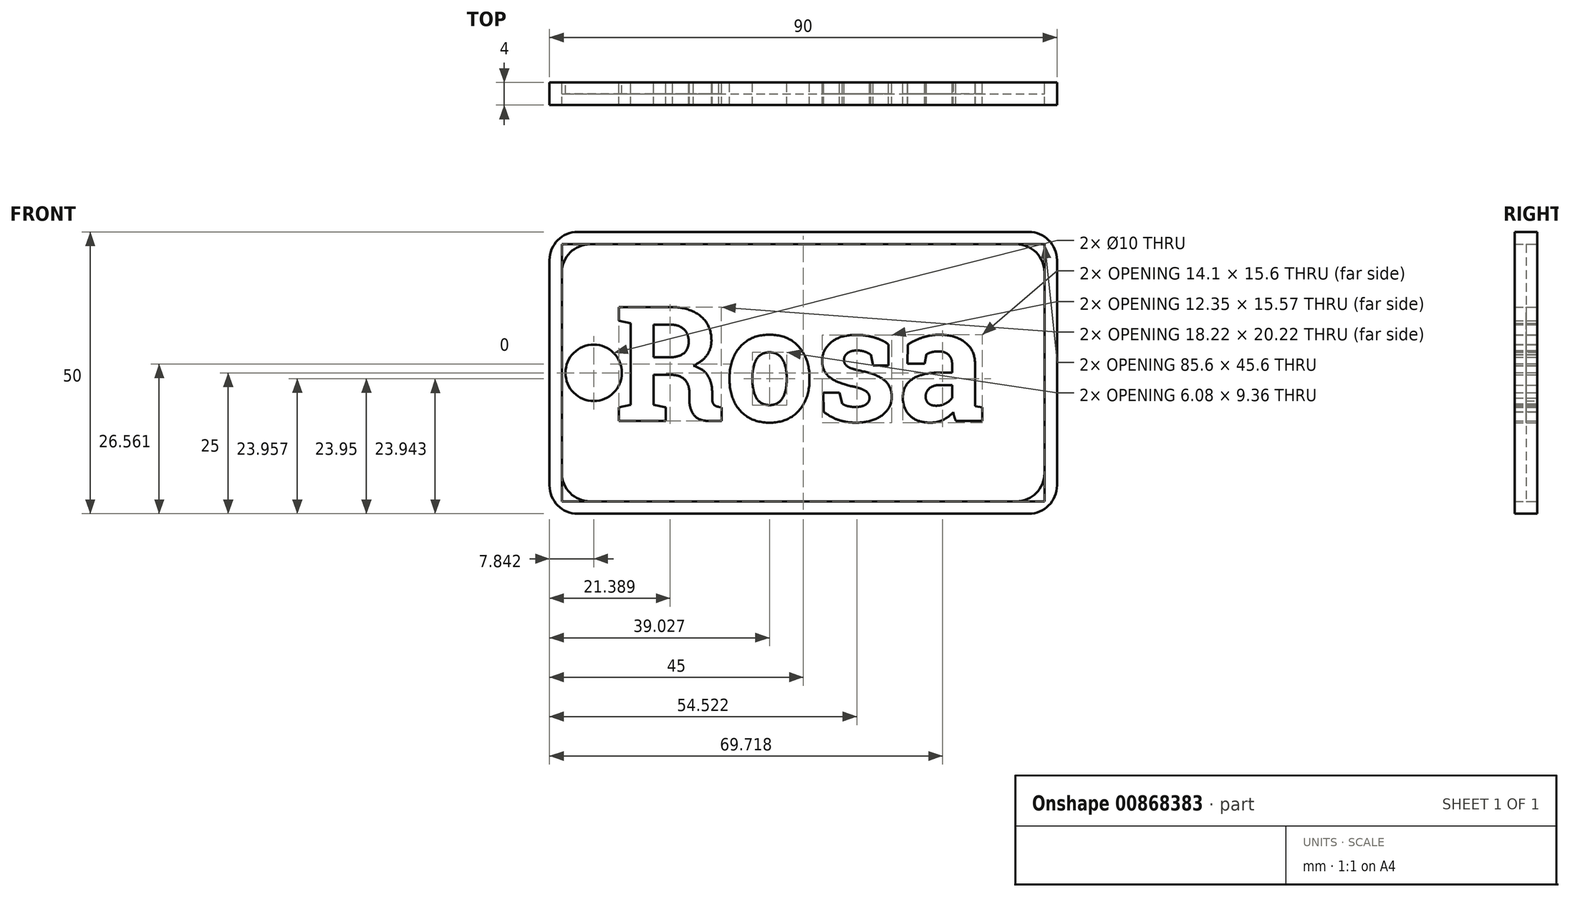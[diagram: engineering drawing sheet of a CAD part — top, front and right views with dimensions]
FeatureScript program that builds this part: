
annotation { "Feature Type Name" : "Feature", "Feature Type Description" : "" }
export const myFeature = defineFeature(function(context is Context, id is Id, definition is map)
    precondition{}
    {
        {
            var Q0;
            Q0=qCreatedBy(makeId("Front.planeOp"),FACE);
            var sketch = newSketch(context, id + "F0", { "sketchPlane" : qUnion([Q0])});
            skLineSegment(sketch, "E0.bottom", {"start": v(-45, 25) * mm, "end": v(45, 25) * mm});
            skLineSegment(sketch, "E0.top", {"start": v(-45, -25) * mm, "end": v(45, -25) * mm});
            skLineSegment(sketch, "E0.left", {"start": v(-45, 25) * mm, "end": v(-45, -25) * mm});
            skLineSegment(sketch, "E0.right", {"start": v(45, 25) * mm, "end": v(45, -25) * mm});
            skLineSegment(sketch, "E1.0", {"start": v(-42.8, 22.8) * mm, "end": v(42.8, 22.8) * mm});
            skLineSegment(sketch, "E1.1", {"start": v(-42.8, 22.8) * mm, "end": v(-42.8, -22.8) * mm});
            skLineSegment(sketch, "E1.2", {"start": v(-42.8, -22.8) * mm, "end": v(42.8, -22.8) * mm});
            skLineSegment(sketch, "E1.3", {"start": v(42.8, 22.8) * mm, "end": v(42.8, -22.8) * mm});
            skText(sketch, "E2", { "text": "Rosa", "fontName": "RobotoSlab-Bold.ttf"});
            skCircle(sketch, "E3", {"center": v(-37.16, 0) * mm, "radius": 5 * mm});
            const initialGuessF0  = {"E2": [-0.0335, -0.00855, 1, 0, 0.02048]};
            skSetInitialGuess(sketch, initialGuessF0);
            skSolve(sketch);
        }
        {
            var Q0;
            Q0=makeQuery(id+"F0.imprint","IMPRINT",FACE,{"disambiguationData":[TD([[makeQuery(id+"F0.imprint","IMPRINT",EDGE,{"derivedFrom":sQuery(id+"F0.wireOp",EDGE,"E2.sketch_text.stroke-244")}),1.0]])]});
            var Q1;
            Q1=makeQuery(id+"F0.imprint","IMPRINT",FACE,{"disambiguationData":[TD([[makeQuery(id+"F0.imprint","IMPRINT",EDGE,{"derivedFrom":sQuery(id+"F0.wireOp",EDGE,"E2.sketch_text.stroke-218")}),1.0]])]});
            var Q2;
            Q2=makeQuery(id+"F0.imprint","IMPRINT",FACE,{"disambiguationData":[TD([[makeQuery(id+"F0.imprint","IMPRINT",EDGE,{"derivedFrom":sQuery(id+"F0.wireOp",EDGE,"E1.0")}),-1.0]])]});
            var Q3;
            Q3=makeQuery(id+"F0.imprint","IMPRINT",FACE,{"disambiguationData":[TD([[makeQuery(id+"F0.imprint","IMPRINT",EDGE,{"derivedFrom":sQuery(id+"F0.wireOp",EDGE,"E2.sketch_text.stroke-36")}),-1.0]])]});
            var Q4;
            Q4=makeQuery(id+"F0.imprint","IMPRINT",FACE,{"disambiguationData":[TD([[makeQuery(id+"F0.imprint","IMPRINT",EDGE,{"derivedFrom":sQuery(id+"F0.wireOp",EDGE,"E2.sketch_text.stroke-46")}),1.0]])]});
            var Q5;
            Q5=makeQuery(id+"F0.imprint","IMPRINT",FACE,{"disambiguationData":[TD([[makeQuery(id+"F0.imprint","IMPRINT",EDGE,{"derivedFrom":sQuery(id+"F0.wireOp",EDGE,"E2.sketch_text.stroke-29")}),1.0]])]});
            var Q6;
            Q6=makeQuery(id+"F0.imprint","IMPRINT",FACE,{"disambiguationData":[TD([[makeQuery(id+"F0.imprint","IMPRINT",EDGE,{"derivedFrom":sQuery(id+"F0.wireOp",EDGE,"E2.sketch_text.stroke-113")}),1.0]])]});
            extrude(context, id + "F1", {"entities" : qUnion([Q0, Q1, Q2, Q3, Q4, Q5, Q6]), "depth" : 2 * mm, "offsetDistance" : 25 * mm});
        }
        {
            var Q0;
            Q0=makeQuery(id+"F0.imprint","IMPRINT",FACE,{"disambiguationData":[TD([[makeQuery(id+"F0.imprint","IMPRINT",EDGE,{"derivedFrom":sQuery(id+"F0.wireOp",EDGE,"E2.sketch_text.stroke-0")}),-1.0]])]});
            var Q1;
            Q1=makeQuery(id+"F0.imprint","IMPRINT",FACE,{"disambiguationData":[TD([[makeQuery(id+"F0.imprint","IMPRINT",EDGE,{"derivedFrom":sQuery(id+"F0.wireOp",EDGE,"E2.sketch_text.stroke-20")}),-1.0]])]});
            var Q2;
            Q2=makeQuery(id+"F0.imprint","IMPRINT",FACE,{"disambiguationData":[TD([[makeQuery(id+"F0.imprint","IMPRINT",EDGE,{"derivedFrom":sQuery(id+"F0.wireOp",EDGE,"E2.sketch_text.stroke-63")}),-1.0]])]});
            var Q3;
            Q3=makeQuery(id+"F0.imprint","IMPRINT",FACE,{"disambiguationData":[TD([[makeQuery(id+"F0.imprint","IMPRINT",EDGE,{"derivedFrom":sQuery(id+"F0.wireOp",EDGE,"E2.sketch_text.stroke-98")}),-1.0]])]});
            var Q4;
            Q4=makeQuery(id+"F0.imprint","IMPRINT",FACE,{"disambiguationData":[TD([[makeQuery(id+"F0.imprint","IMPRINT",EDGE,{"derivedFrom":sQuery(id+"F0.wireOp",EDGE,"E2.sketch_text.stroke-117")}),-1.0]])]});
            var Q5;
            Q5=makeQuery(id+"F0.imprint","IMPRINT",FACE,{"disambiguationData":[TD([[makeQuery(id+"F0.imprint","IMPRINT",EDGE,{"derivedFrom":sQuery(id+"F0.wireOp",EDGE,"E2.sketch_text.stroke-127")}),-1.0]])]});
            var Q6;
            Q6=makeQuery(id+"F0.imprint","IMPRINT",FACE,{"disambiguationData":[TD([[makeQuery(id+"F0.imprint","IMPRINT",EDGE,{"derivedFrom":sQuery(id+"F0.wireOp",EDGE,"E2.sketch_text.stroke-131")}),-1.0]])]});
            var Q7;
            Q7=makeQuery(id+"F0.imprint","IMPRINT",FACE,{"disambiguationData":[TD([[makeQuery(id+"F0.imprint","IMPRINT",EDGE,{"derivedFrom":sQuery(id+"F0.wireOp",EDGE,"E2.sketch_text.stroke-141")}),-1.0]])]});
            var Q8;
            Q8=makeQuery(id+"F0.imprint","IMPRINT",FACE,{"disambiguationData":[TD([[makeQuery(id+"F0.imprint","IMPRINT",EDGE,{"derivedFrom":sQuery(id+"F0.wireOp",EDGE,"E2.sketch_text.stroke-151")}),-1.0]])]});
            var Q9;
            Q9=makeQuery(id+"F0.imprint","IMPRINT",FACE,{"disambiguationData":[TD([[makeQuery(id+"F0.imprint","IMPRINT",EDGE,{"derivedFrom":sQuery(id+"F0.wireOp",EDGE,"E2.sketch_text.stroke-254")}),-1.0]])]});
            var Q10;
            Q10=makeQuery(id+"F0.imprint","IMPRINT",FACE,{"disambiguationData":[TD([[makeQuery(id+"F0.imprint","IMPRINT",EDGE,{"derivedFrom":sQuery(id+"F0.wireOp",EDGE,"E2.sketch_text.stroke-225")}),-1.0]])]});
            var Q11;
            Q11=makeQuery(id+"F0.imprint","IMPRINT",FACE,{"disambiguationData":[TD([[makeQuery(id+"F0.imprint","IMPRINT",EDGE,{"derivedFrom":sQuery(id+"F0.wireOp",EDGE,"E2.sketch_text.stroke-201")}),-1.0]])]});
            var Q12;
            Q12=makeQuery(id+"F0.imprint","IMPRINT",FACE,{"disambiguationData":[TD([[makeQuery(id+"F0.imprint","IMPRINT",EDGE,{"derivedFrom":sQuery(id+"F0.wireOp",EDGE,"E2.sketch_text.stroke-171")}),-1.0]])]});
            var Q13;
            Q13=makeQuery(id+"F0.imprint","IMPRINT",FACE,{"disambiguationData":[TD([[makeQuery(id+"F0.imprint","IMPRINT",EDGE,{"derivedFrom":sQuery(id+"F0.wireOp",EDGE,"E0.bottom")}),-1.0]])]});
            var Q14;
            Q14=makeQuery(id+"F0.imprint","IMPRINT",FACE,{"disambiguationData":[TD([[makeQuery(id+"F0.imprint","IMPRINT",EDGE,{"derivedFrom":sQuery(id+"F0.wireOp",EDGE,"E2.sketch_text.stroke-36")}),-1.0]])]});
            extrude(context, id + "F2", {"entities" : qUnion([Q0, Q1, Q2, Q3, Q4, Q5, Q6, Q7, Q8, Q9, Q10, Q11, Q12, Q13, Q14]), "depth" : 4 * mm, "offsetDistance" : 25 * mm});
        }
        {
            var Q0;
            Q0=makeQuery(id+"F2.opExtrude","SWEPT_EDGE",EDGE,{"disambiguationData":[OSD([sQuery(id+"F0.wireOp",EDGE,"E0.top"),sQuery(id+"F0.wireOp",EDGE,"E0.left")])]});
            var Q1;
            Q1=makeQuery(id+"F2.opExtrude","SWEPT_EDGE",EDGE,{"disambiguationData":[OSD([sQuery(id+"F0.wireOp",EDGE,"E0.bottom"),sQuery(id+"F0.wireOp",EDGE,"E0.left")])]});
            var Q2;
            Q2=makeQuery(id+"F2.opExtrude","SWEPT_EDGE",EDGE,{"disambiguationData":[OSD([sQuery(id+"F0.wireOp",EDGE,"E1.1"),sQuery(id+"F0.wireOp",EDGE,"E1.2")])]});
            var Q3;
            Q3=makeQuery(id+"F2.opExtrude","SWEPT_EDGE",EDGE,{"disambiguationData":[OSD([sQuery(id+"F0.wireOp",EDGE,"E1.0"),sQuery(id+"F0.wireOp",EDGE,"E1.1")])]});
            var Q4;
            Q4=makeQuery(id+"F2.opExtrude","SWEPT_EDGE",EDGE,{"disambiguationData":[OSD([sQuery(id+"F0.wireOp",EDGE,"E1.0"),sQuery(id+"F0.wireOp",EDGE,"E1.3")])]});
            var Q5;
            Q5=makeQuery(id+"F2.opExtrude","SWEPT_EDGE",EDGE,{"disambiguationData":[OSD([sQuery(id+"F0.wireOp",EDGE,"E1.2"),sQuery(id+"F0.wireOp",EDGE,"E1.3")])]});
            var Q6;
            Q6=makeQuery(id+"F2.opExtrude","SWEPT_EDGE",EDGE,{"disambiguationData":[OSD([sQuery(id+"F0.wireOp",EDGE,"E0.top"),sQuery(id+"F0.wireOp",EDGE,"E0.right")])]});
            var Q7;
            Q7=makeQuery(id+"F2.opExtrude","SWEPT_EDGE",EDGE,{"disambiguationData":[OSD([sQuery(id+"F0.wireOp",EDGE,"E0.bottom"),sQuery(id+"F0.wireOp",EDGE,"E0.right")])]});
            fillet(context, id + "F3", {"entities" : qUnion([Q0, Q1, Q2, Q3, Q4, Q5, Q6, Q7]), "radius" : 5 * mm, "tangentPropagation" : true, "allowEdgeOverflow" : false});
        }
    });
